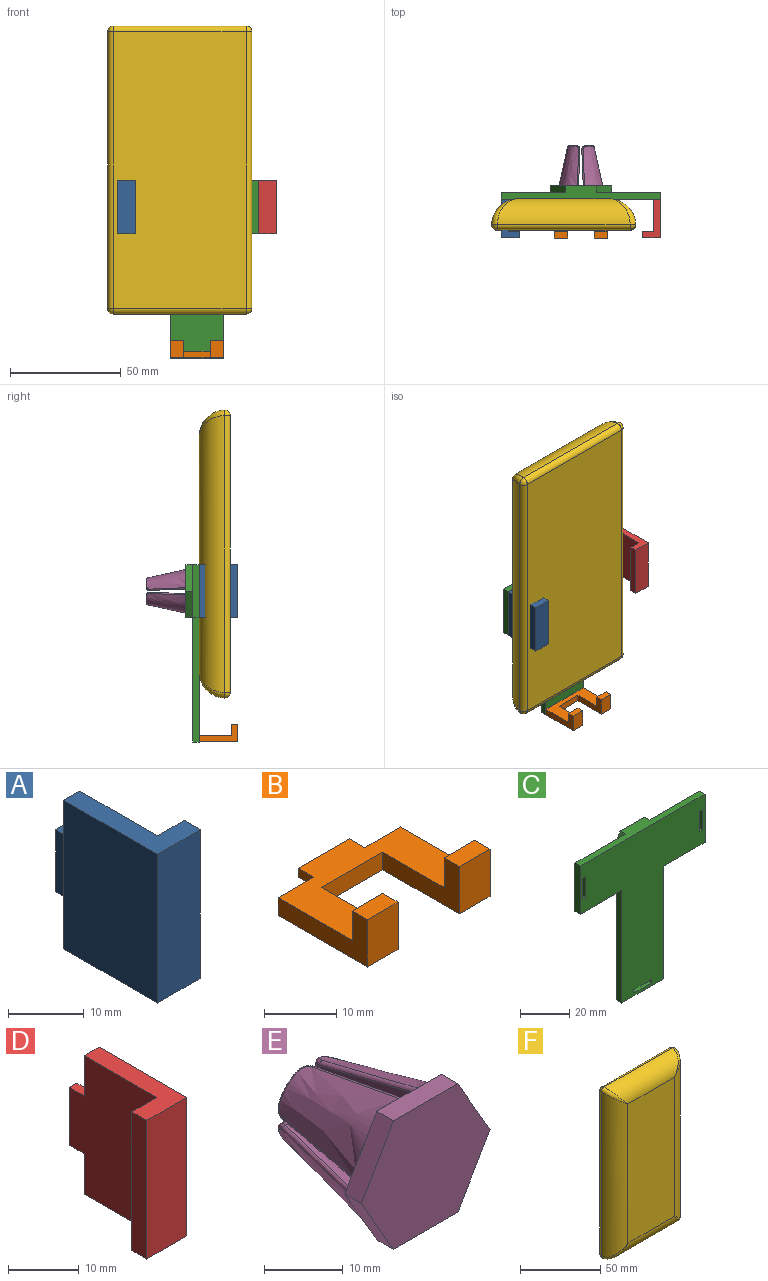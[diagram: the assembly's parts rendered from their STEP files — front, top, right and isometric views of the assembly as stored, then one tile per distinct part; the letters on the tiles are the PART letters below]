
ASSEMBLY  parts=6 mates=5
PART A: 12 faces, bbox 8x20.5x24 mm
  f0: plane 17.5x8mm, normal (0,0,-1), area 67.5mm2, adj f1,f4,f5,f6,f7,f11
  f1: plane 24x17.5mm, normal (1,0,0), area 378mm2, adj f0,f2,f3,f7,f8,f10,f11
  f2: plane 17.5x8mm, normal (0,0,1), area 67.5mm2, adj f1,f4,f5,f6,f7,f11
  f3: plane 10x1.5mm, normal (0,1,0), area 15mm2, adj f1,f8,f9,f10
  f4: plane 24x17.5mm, normal (-1,0,0), area 420mm2, adj f0,f2,f6,f11
  f5: plane 24x3mm, normal (1,0,0), area 72mm2, adj f0,f2,f6,f7
  f6: plane 24x8mm, normal (0,-1,0), area 192mm2, adj f0,f2,f4,f5
  f7: plane 24x5mm, normal (0,1,0), area 120mm2, adj f0,f1,f2,f5
  f8: plane 3x1.5mm, normal (0,0,1), area 4.5mm2, adj f1,f3,f9,f11
  f9: plane 10x3mm, normal (-1,0,0), area 30mm2, adj f3,f8,f10,f11
  f10: plane 3x1.5mm, normal (0,0,-1), area 4.5mm2, adj f1,f3,f9,f11
  f11: plane 24x3mm, normal (0,1,0), area 57mm2, adj f0,f1,f2,f4,f8,f9,f10
PART B: 18 faces, bbox 24x20.5x8 mm
  f0: plane 10x1.5mm, normal (0,1,0), area 15mm2, adj f1,f2,f3,f4
  f1: plane 24x17.5mm, normal (0,0,1), area 234mm2, adj f0,f3,f4,f5,f6,f7,f9,f12
  f2: plane 10x3mm, normal (0,0,-1), area 30mm2, adj f0,f3,f4,f5
  f3: plane 3x1.5mm, normal (-1,0,0), area 4.5mm2, adj f0,f1,f2,f5
  f4: plane 3x1.5mm, normal (1,0,0), area 4.5mm2, adj f0,f1,f2,f5
  f5: plane 24x3mm, normal (0,1,0), area 57mm2, adj f1,f2,f3,f4,f7,f8,f16
  f6: plane 15x8mm, normal (1,0,0), area 60mm2, adj f1,f8,f9,f10,f11,f17
  f7: plane 17.5x8mm, normal (-1,0,0), area 67.5mm2, adj f1,f5,f8,f9,f10,f11
  f8: plane 24x17.5mm, normal (0,0,-1), area 240mm2, adj f5,f6,f7,f11,f12,f15,f16,f17
  f9: plane 6x5mm, normal (0,1,0), area 30mm2, adj f1,f6,f7,f10
  f10: plane 6x3mm, normal (0,0,1), area 18mm2, adj f6,f7,f9,f11
  f11: plane 8x6mm, normal (0,-1,0), area 48mm2, adj f6,f7,f8,f10
  f12: plane 15x8mm, normal (-1,0,0), area 60mm2, adj f1,f8,f13,f14,f15,f17
  f13: plane 6x5mm, normal (0,1,0), area 30mm2, adj f1,f12,f14,f16
  f14: plane 6x3mm, normal (0,0,1), area 18mm2, adj f12,f13,f15,f16
  f15: plane 8x6mm, normal (0,-1,0), area 48mm2, adj f8,f12,f14,f16
  f16: plane 17.5x8mm, normal (1,0,0), area 67.5mm2, adj f1,f5,f8,f13,f14,f15
  f17: plane 12x3mm, normal (0,-1,0), area 36mm2, adj f1,f6,f8,f12
PART C: 35 faces, bbox 71.7x6x80 mm
  f0: plane 56x3mm, normal (-1,0,0), area 168mm2, adj f2,f3,f4,f5
  f1: plane 56x3mm, normal (1,0,0), area 168mm2, adj f2,f3,f4,f9
  f2: plane 24x3mm, normal (0,0,-1), area 72mm2, adj f0,f1,f3,f4
  f3: plane 80x71.7mm, normal (0,1,0), area 2517.5mm2, adj f0,f1,f2,f5,f6,f7,f8,f9
  f4: plane 80x71.7mm, normal (0,-1,0), area 3016.3mm2, adj f0,f1,f2,f5,f6,f7,f8,f9
  f5: plane 23.85x3mm, normal (0,0,-1), area 71.5mm2, adj f0,f3,f4,f8
  f6: plane 24x3mm, normal (1,0,0), area 72mm2, adj f3,f4,f7,f9
  f7: plane 71.7x6mm, normal (0,0,1), area 256.7mm2, adj f3,f4,f6,f8,f16,f17,f21
  f8: plane 24x3mm, normal (-1,0,0), area 72mm2, adj f3,f4,f5,f7
  f9: plane 23.85x3mm, normal (0,0,-1), area 71.5mm2, adj f1,f3,f4,f6
  f10: plane 10.1x5.83mm, normal (0.87,0,-0.5), area 35mm2, adj f11,f20,f21,f22
  f11: plane 10.1x5.83mm, normal (0.87,0,0.5), area 35mm2, adj f10,f12,f21,f22
  f12: plane 11.66x3mm, normal (0,0,1), area 35mm2, adj f11,f13,f21,f22
  f13: plane 10.1x5.83mm, normal (-0.87,0,0.5), area 35mm2, adj f12,f14,f21,f22
  f14: plane 10.1x5.83mm, normal (-0.87,0,-0.5), area 35mm2, adj f13,f20,f21,f22
  f15: plane 12x6.93mm, normal (-0.87,0,-0.5), area 41.6mm2, adj f3,f16,f19,f21
  f16: plane 12x6.93mm, normal (-0.87,0,0.5), area 41.6mm2, adj f3,f7,f15,f21
  f17: plane 12x6.93mm, normal (0.87,0,0.5), area 41.6mm2, adj f3,f7,f18,f21
  f18: plane 12x6.93mm, normal (0.87,0,-0.5), area 41.6mm2, adj f3,f17,f19,f21
  f19: plane 13.86x3mm, normal (0,0,-1), area 41.6mm2, adj f3,f15,f18,f21
  f20: plane 11.66x3mm, normal (0,0,-1), area 35mm2, adj f10,f14,f21,f22
  f21: plane 27.71x24mm, normal (0,1,0), area 145.5mm2, adj f7,f10,f11,f12,f13,f14,f15,f16
  f22: plane 23.33x20.2mm, normal (0,1,0), area 353.4mm2, adj f10,f11,f12,f13,f14,f20
  f23: plane 10.1x3mm, normal (1,0,0), area 30.3mm2, adj f3,f4,f24,f25
  f24: plane 3x1.6mm, normal (0,0,-1), area 4.8mm2, adj f3,f4,f23,f26
  f25: plane 3x1.6mm, normal (0,0,1), area 4.8mm2, adj f3,f4,f23,f26
  f26: plane 10.1x3mm, normal (-1,0,0), area 30.3mm2, adj f3,f4,f24,f25
  f27: plane 10.1x3mm, normal (0,0,1), area 30.3mm2, adj f3,f4,f28,f29
  f28: plane 3x1.6mm, normal (1,0,0), area 4.8mm2, adj f3,f4,f27,f30
  f29: plane 3x1.6mm, normal (-1,0,0), area 4.8mm2, adj f3,f4,f27,f30
  f30: plane 10.1x3mm, normal (0,0,-1), area 30.3mm2, adj f3,f4,f28,f29
  f31: plane 10.1x3mm, normal (1,0,0), area 30.3mm2, adj f3,f4,f32,f33
  f32: plane 3x1.6mm, normal (0,0,-1), area 4.8mm2, adj f3,f4,f31,f34
  f33: plane 3x1.6mm, normal (0,0,1), area 4.8mm2, adj f3,f4,f31,f34
  f34: plane 10.1x3mm, normal (-1,0,0), area 30.3mm2, adj f3,f4,f32,f33
PART D: 12 faces, bbox 8x20.5x24 mm
  f0: plane 17.5x8mm, normal (0,0,-1), area 67.5mm2, adj f1,f3,f5,f6,f7,f11
  f1: plane 24x17.5mm, normal (1,0,0), area 420mm2, adj f0,f4,f6,f11
  f2: plane 10x1.5mm, normal (0,1,0), area 15mm2, adj f3,f8,f9,f10
  f3: plane 24x17.5mm, normal (-1,0,0), area 378mm2, adj f0,f2,f4,f7,f8,f10,f11
  f4: plane 17.5x8mm, normal (0,0,1), area 67.5mm2, adj f1,f3,f5,f6,f7,f11
  f5: plane 24x3mm, normal (-1,0,0), area 72mm2, adj f0,f4,f6,f7
  f6: plane 24x8mm, normal (0,-1,0), area 192mm2, adj f0,f1,f4,f5
  f7: plane 24x5mm, normal (0,1,0), area 120mm2, adj f0,f3,f4,f5
  f8: plane 3x1.5mm, normal (0,0,-1), area 4.5mm2, adj f2,f3,f9,f11
  f9: plane 10x3mm, normal (1,0,0), area 30mm2, adj f2,f8,f10,f11
  f10: plane 3x1.5mm, normal (0,0,1), area 4.5mm2, adj f2,f3,f9,f11
  f11: plane 24x3mm, normal (0,1,0), area 57mm2, adj f0,f1,f3,f4,f8,f9,f10
PART E: 60 faces, bbox 23.1x23.3x21 mm
  f0: bspline ~17.61x9.12mm, area 179.4mm2, adj f4,f18,f19,f20,f48,f52
  f1: bspline ~17.61x9.12mm, area 179.4mm2, adj f4,f22,f23,f24,f43,f47
  f2: bspline ~17.61x9.12mm, area 179.4mm2, adj f4,f26,f27,f28,f38,f42
  f3: bspline ~17.61x9.12mm, area 179.4mm2, adj f4,f30,f31,f32,f33,f37
  f4: plane 23.15x20.05mm, normal (0,1,0), area 112.5mm2, adj f0,f1,f2,f3,f6,f7,f9,f10
  f5: plane 3.36x3.36mm, normal (0,1,0), area 7.3mm2, adj f31,f34,f36
  f6: plane 16.44x8.45mm, normal (-1,-0.04,0), area 104.1mm2, adj f4,f29,f32,f34
  f7: plane 16.44x8.45mm, normal (0,-0.04,-1), area 104.1mm2, adj f4,f29,f30,f36
  f8: plane 3.36x3.36mm, normal (0,1,0), area 7.3mm2, adj f27,f39,f41
  f9: plane 16.44x8.45mm, normal (1,-0.04,0), area 104.1mm2, adj f4,f25,f28,f39
  f10: plane 16.44x8.45mm, normal (0,-0.04,-1), area 104.1mm2, adj f4,f25,f26,f41
  f11: plane 3.36x3.36mm, normal (0,1,0), area 7.3mm2, adj f23,f44,f46
  f12: plane 16.44x8.45mm, normal (-1,-0.04,0), area 104.1mm2, adj f4,f21,f24,f44
  f13: plane 16.44x8.45mm, normal (0,-0.04,1), area 104.1mm2, adj f4,f21,f22,f46
  f14: plane 3.36x3.36mm, normal (0,1,0), area 7.3mm2, adj f19,f49,f51
  f15: plane 16.44x8.45mm, normal (0,-0.04,1), area 104.1mm2, adj f4,f17,f20,f49
  f16: plane 16.44x8.45mm, normal (1,-0.04,0), area 104.1mm2, adj f4,f17,f18,f51
  f17: cylinder r=0.5mm len=16.45mm, axis (-0.04,-1,-0.04), area 12.9mm2, adj f4,f15,f16,f50
  f18: bspline ~22.67x5.51mm, area 14.7mm2, adj f0,f4,f16,f52
  f19: bspline ~4.84x4.73mm, area 3.5mm2, adj f0,f14,f48,f52
  f20: bspline ~22.67x5.51mm, area 14.7mm2, adj f0,f4,f15,f48
  f21: cylinder r=0.5mm len=16.45mm, axis (0.04,-1,-0.04), area 12.9mm2, adj f4,f12,f13,f45
  f22: bspline ~22.67x5.51mm, area 14.7mm2, adj f1,f4,f13,f47
  f23: bspline ~4.84x4.73mm, area 3.5mm2, adj f1,f11,f43,f47
  f24: bspline ~22.67x5.51mm, area 14.7mm2, adj f1,f4,f12,f43
  f25: cylinder r=0.5mm len=16.45mm, axis (-0.04,-1,0.04), area 12.9mm2, adj f4,f9,f10,f40
  f26: bspline ~22.67x5.51mm, area 14.7mm2, adj f2,f4,f10,f42
  f27: bspline ~4.84x4.73mm, area 3.5mm2, adj f2,f8,f38,f42
  f28: bspline ~22.67x5.51mm, area 14.7mm2, adj f2,f4,f9,f38
  f29: cylinder r=0.5mm len=16.45mm, axis (-0.04,1,-0.04), area 12.9mm2, adj f4,f6,f7,f35
  f30: bspline ~20.1x4.95mm, area 14.7mm2, adj f3,f4,f7,f37
  f31: bspline ~4.6x4.37mm, area 3.5mm2, adj f3,f5,f33,f37
  f32: bspline ~20.1x4.95mm, area 14.7mm2, adj f3,f4,f6,f33
  f33: bspline ~1.97x1.66mm, area 1.7mm2, adj f3,f31,f32,f34
  f34: cylinder r=1.5mm len=4.85mm, axis (0,0,-1), area 9.9mm2, adj f5,f6,f33,f35
  f35: bspline ~1.76x1.5mm, area 0.8mm2, adj f29,f34,f36
  f36: cylinder r=1.5mm len=4.85mm, axis (-1,0,0), area 9.9mm2, adj f5,f7,f35,f37
  f37: bspline ~1.93x1.89mm, area 1.7mm2, adj f3,f30,f31,f36
  f38: bspline ~1.93x1.89mm, area 1.7mm2, adj f2,f27,f28,f39
  f39: cylinder r=1.5mm len=4.85mm, axis (0,0,-1), area 9.9mm2, adj f8,f9,f38,f40
  f40: bspline ~1.76x1.5mm, area 0.8mm2, adj f25,f39,f41
  f41: cylinder r=1.5mm len=4.85mm, axis (1,0,0), area 9.9mm2, adj f8,f10,f40,f42
  f42: bspline ~1.97x1.66mm, area 1.7mm2, adj f2,f26,f27,f41
  f43: bspline ~1.93x1.89mm, area 1.7mm2, adj f1,f23,f24,f44
  f44: cylinder r=1.5mm len=4.85mm, axis (0,0,1), area 9.9mm2, adj f11,f12,f43,f45
  f45: bspline ~1.76x1.5mm, area 0.8mm2, adj f21,f44,f46
  f46: cylinder r=1.5mm len=4.85mm, axis (-1,0,0), area 9.9mm2, adj f11,f13,f45,f47
  f47: bspline ~1.97x1.66mm, area 1.7mm2, adj f1,f22,f23,f46
  f48: bspline ~1.93x1.89mm, area 1.7mm2, adj f0,f19,f20,f49
  f49: cylinder r=1.5mm len=4.85mm, axis (1,0,0), area 9.9mm2, adj f14,f15,f48,f50
  f50: bspline ~1.76x1.5mm, area 0.8mm2, adj f17,f49,f51
  f51: cylinder r=1.5mm len=4.85mm, axis (0,0,1), area 9.9mm2, adj f14,f16,f50,f52
  f52: bspline ~1.97x1.66mm, area 1.7mm2, adj f0,f18,f19,f51
  f53: plane 11.55x3mm, normal (0,0,1), area 34.6mm2, adj f4,f54,f58,f59
  f54: plane 10x5.77mm, normal (0.87,0,0.5), area 34.6mm2, adj f4,f53,f55,f59
  f55: plane 10x5.77mm, normal (0.87,0,-0.5), area 34.6mm2, adj f4,f54,f56,f59
  f56: plane 11.55x3mm, normal (0,0,-1), area 34.6mm2, adj f4,f55,f57,f59
  f57: plane 10x5.77mm, normal (-0.87,0,-0.5), area 34.6mm2, adj f4,f56,f58,f59
  f58: plane 10x5.77mm, normal (-0.87,0,0.5), area 34.6mm2, adj f4,f53,f57,f59
  f59: plane 23.09x20mm, normal (0,-1,0), area 346.4mm2, adj f53,f54,f55,f56,f57,f58
PART F: 18 faces, bbox 65x14x130 mm
  f0: plane 106.02x41.02mm, normal (0,-1,0), area 4349.1mm2, adj f10,f13,f14,f17
  f1: plane 125x60mm, normal (0,1,0), area 7500mm2, adj f3,f4,f7,f8
  f2: sphere r=2.5mm, area 9.8mm2, adj f3,f4,f11
  f3: cylinder r=2.5mm len=60mm, axis (-1,0,0), area 235.6mm2, adj f1,f2,f5,f13
  f4: cylinder r=2.5mm len=125mm, axis (0,0,-1), area 490.9mm2, adj f1,f2,f6,f10
  f5: sphere r=2.5mm, area 13.4mm2, adj f3,f7,f15
  f6: sphere r=2.5mm, area 9.8mm2, adj f4,f8,f12
  f7: cylinder r=2.5mm len=125mm, axis (0,0,1), area 490.9mm2, adj f1,f5,f9,f17
  f8: cylinder r=2.5mm len=60mm, axis (1,0,0), area 235.6mm2, adj f1,f6,f9,f14
  f9: sphere r=2.5mm, area 6.2mm2, adj f7,f8,f16
  f10: cylinder r=12mm len=125mm, axis (0,0,-1), area 2119.5mm2, adj f0,f4,f11,f12
  f11: bspline ~11.99x11.99mm, area 31mm2, adj f2,f10,f13
  f12: bspline ~11.99x11.99mm, area 31mm2, adj f6,f10,f14
  f13: cylinder r=12mm len=60mm, axis (1,0,0), area 926.8mm2, adj f0,f3,f11,f15
  f14: cylinder r=12mm len=60mm, axis (1,0,0), area 926.8mm2, adj f0,f8,f12,f16
  f15: bspline ~11.99x11.99mm, area 31mm2, adj f5,f13,f17
  f16: bspline ~11.99x11.99mm, area 31mm2, adj f9,f14,f17
  f17: cylinder r=12mm len=125mm, axis (0,0,-1), area 2119.5mm2, adj f0,f7,f15,f16
PLACE A t=(-81.2,-40.39,27.55)mm
PLACE B t=(-94.2,-40.39,40.65)mm
PLACE C t=(-94.2,-40.39,27.55)mm
PLACE D t=(-107.2,-40.39,27.55)mm
PLACE E t=(-94.2,-57.39,27.55)mm
PLACE F rot(axis=(1,0,0),180deg) t=(-237.27,-74.39,1.55)mm
MATE fastened B.f0 <-> C.f3  axis (0,1,0) through (-94.2,-57.39,-37.35)mm
MATE fastened E.f59 <-> C.f22  axis (0,-1,0) through (-94.2,-57.39,27.55)mm
MATE planar C.f4 <-> F.f0  axis (0,-1,0) through (-94.2,-60.39,10.08)mm
MATE fastened D.f2 <-> C.f3  axis (0,1,0) through (-59.85,-57.39,27.55)mm
MATE fastened A.f3 <-> C.f3  axis (0,1,0) through (-128.55,-57.39,27.55)mm
